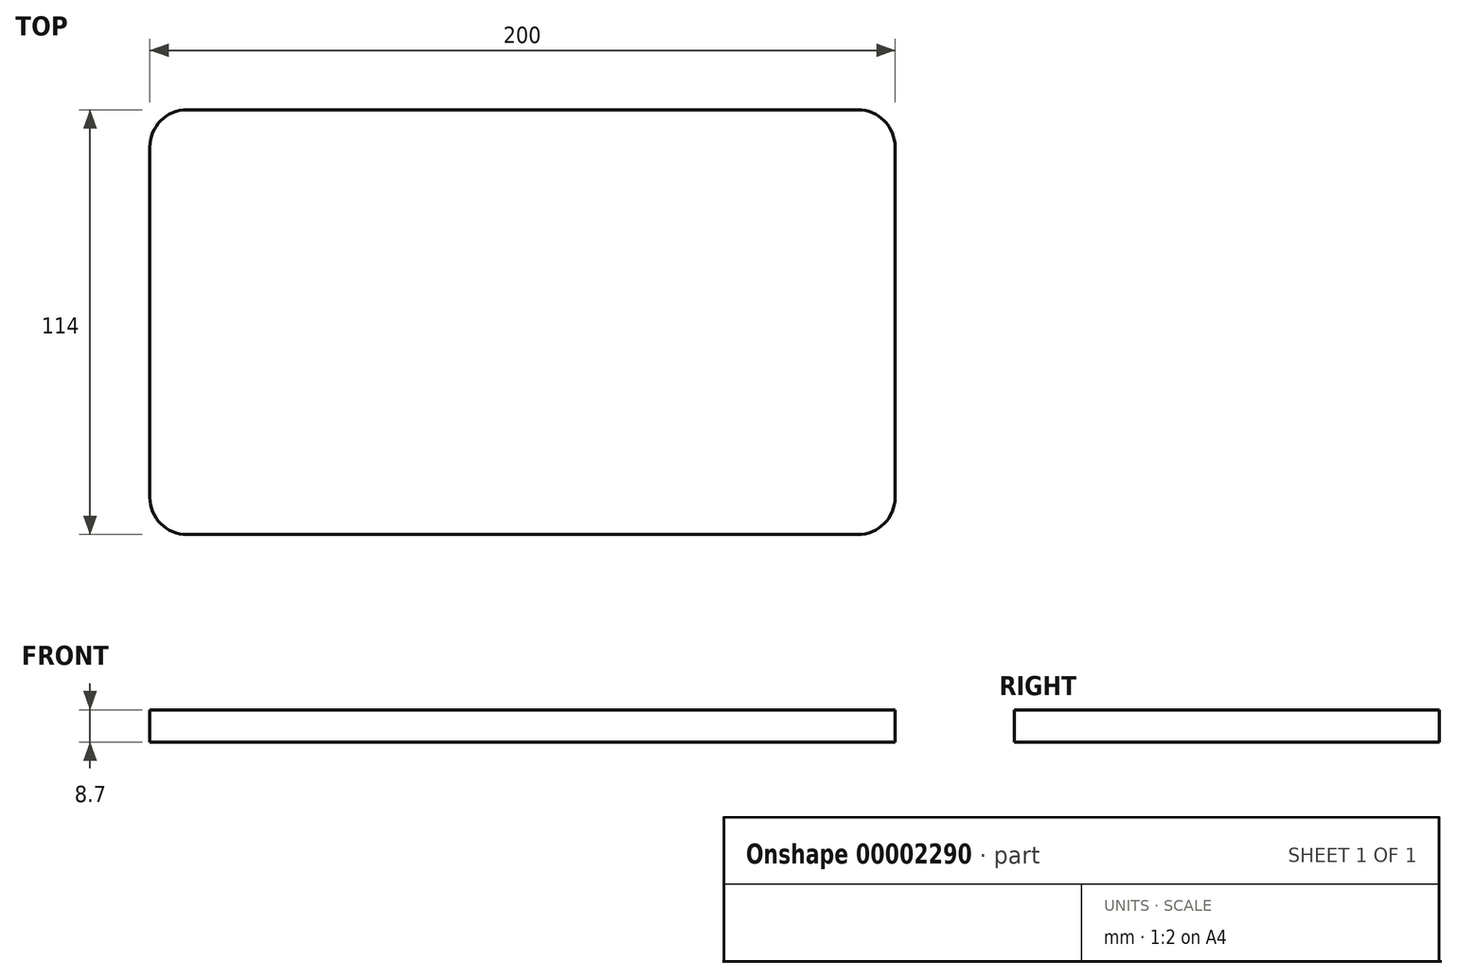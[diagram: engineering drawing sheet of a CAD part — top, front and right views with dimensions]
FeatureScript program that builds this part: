
annotation { "Feature Type Name" : "Feature", "Feature Type Description" : "" }
export const myFeature = defineFeature(function(context is Context, id is Id, definition is map)
    precondition{}
    {
        {
            var Q0;
            Q0=qCreatedBy(makeId("Top.planeOp"),FACE);
            var sketch = newSketch(context, id + "F0", { "sketchPlane" : qUnion([Q0])});
            skLineSegment(sketch, "E0.rect.bottom", {"start": v(90, 57) * mm, "end": v(-90, 57) * mm});
            skLineSegment(sketch, "E0.rect.top", {"start": v(90, -57) * mm, "end": v(-90, -57) * mm});
            skLineSegment(sketch, "E0.rect.left", {"start": v(100, 47) * mm, "end": v(100, -47) * mm});
            skLineSegment(sketch, "E0.rect.right", {"start": v(-100, 47) * mm, "end": v(-100, -47) * mm});
            skPoint(sketch, "E0.rect.middle", {"position": v(0, 0) * mm});
            skPoint(sketch, "E1.visualSharp", {"position": v(-100, 57) * mm});
            skArc(sketch, "E1.filletArc", {"start": v(-90, 57) * mm, "mid": v(-97.07, 54.07) * mm, "end": v(-100, 47) * mm});
            skPoint(sketch, "E2.visualSharp", {"position": v(100, 57) * mm});
            skArc(sketch, "E2.filletArc", {"start": v(100, 47) * mm, "mid": v(97.07, 54.07) * mm, "end": v(90, 57) * mm});
            skPoint(sketch, "E3.visualSharp", {"position": v(100, -57) * mm});
            skArc(sketch, "E3.filletArc", {"start": v(90, -57) * mm, "mid": v(97.07, -54.07) * mm, "end": v(100, -47) * mm});
            skPoint(sketch, "E4.visualSharp", {"position": v(-100, -57) * mm});
            skArc(sketch, "E4.filletArc", {"start": v(-100, -47) * mm, "mid": v(-97.07, -54.07) * mm, "end": v(-90, -57) * mm});
            skSolve(sketch);
        }
        {
            var Q0;
            Q0=makeQuery(id+"F0.imprint","IMPRINT",FACE,{"disambiguationData":[TD([[makeQuery(id+"F0.imprint","IMPRINT",EDGE,{"derivedFrom":sQuery(id+"F0.wireOp",EDGE,"E0.rect.bottom")}),1.0]])]});
            extrude(context, id + "F1", {"entities" : qUnion([Q0]), "depth" : 8.7 * mm});
        }
    });
